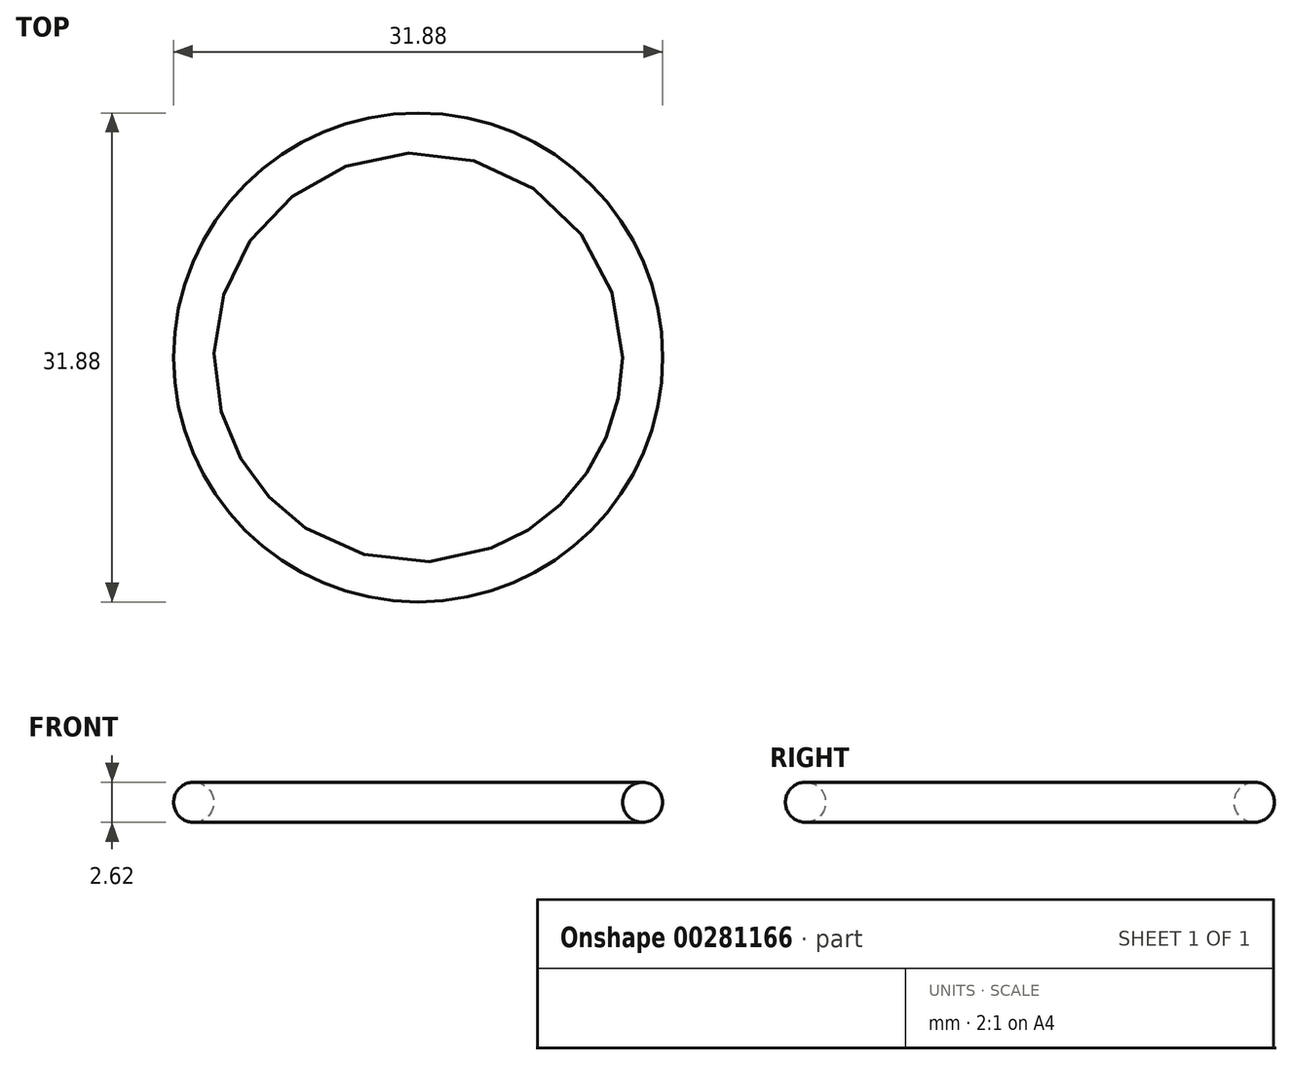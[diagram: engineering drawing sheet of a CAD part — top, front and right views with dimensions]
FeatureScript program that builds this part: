
annotation { "Feature Type Name" : "Feature", "Feature Type Description" : "" }
export const myFeature = defineFeature(function(context is Context, id is Id, definition is map)
    precondition{}
    {
        {
            assignVariable(context, id + "F0", {"name" : "CS", "anyValue" : .103});
        }
        {
            var Q0;
            Q0=qCreatedBy(makeId("Top.planeOp"),FACE);
            cPlane(context, id + "F1", {"entities" : qUnion([Q0]), "cplaneType" : CPlaneType.OFFSET, "offset" : (getVariable(context, 'CS')) * mm, "oppositeDirection" : true, "width" : 152.4 * mm, "height" : 152.4 * mm});
        }
        {
            var Q0;
            Q0=qCreatedBy(makeId("Front.planeOp"),FACE);
            var sketch = newSketch(context, id + "F2", { "sketchPlane" : qUnion([Q0])});
            skLineSegment(sketch, "E0", {"start": v(0, 0) * mm, "end": v(0, -2.62) * mm, "construction": true});
            skLineSegment(sketch, "E1", {"start": v(0, -2.62) * mm, "end": v(13.32, -2.62) * mm, "construction": true});
            skLineSegment(sketch, "E2", {"start": v(13.32, 0) * mm, "end": v(0, 0) * mm, "construction": true});
            skCircle(sketch, "E3", {"center": v(14.63, -1.3) * mm, "radius": 1.3 * mm});
            skLineSegment(sketch, "E4", {"start": v(13.32, -1.3) * mm, "end": v(14.63, -1.3) * mm, "construction": true});
            skLineSegment(sketch, "E5", {"start": v(13.32, 0) * mm, "end": v(13.32, -1.3) * mm, "construction": true});
            skLineSegment(sketch, "E6", {"start": v(13.32, -2.62) * mm, "end": v(13.32, -1.3) * mm, "construction": true});
            skSolve(sketch);
        }
        {
            var Q0;
            Q0=qSketchRegion(id+"F2",true);
            var Q1;
            Q1=sQuery(id+"F2.wireOp",EDGE,"E0");
            revolve(context, id + "F3", {"entities" : qUnion([Q0]), "axis" : qUnion([Q1]), "revolveType" : RevolveType.FULL});
        }
    });
